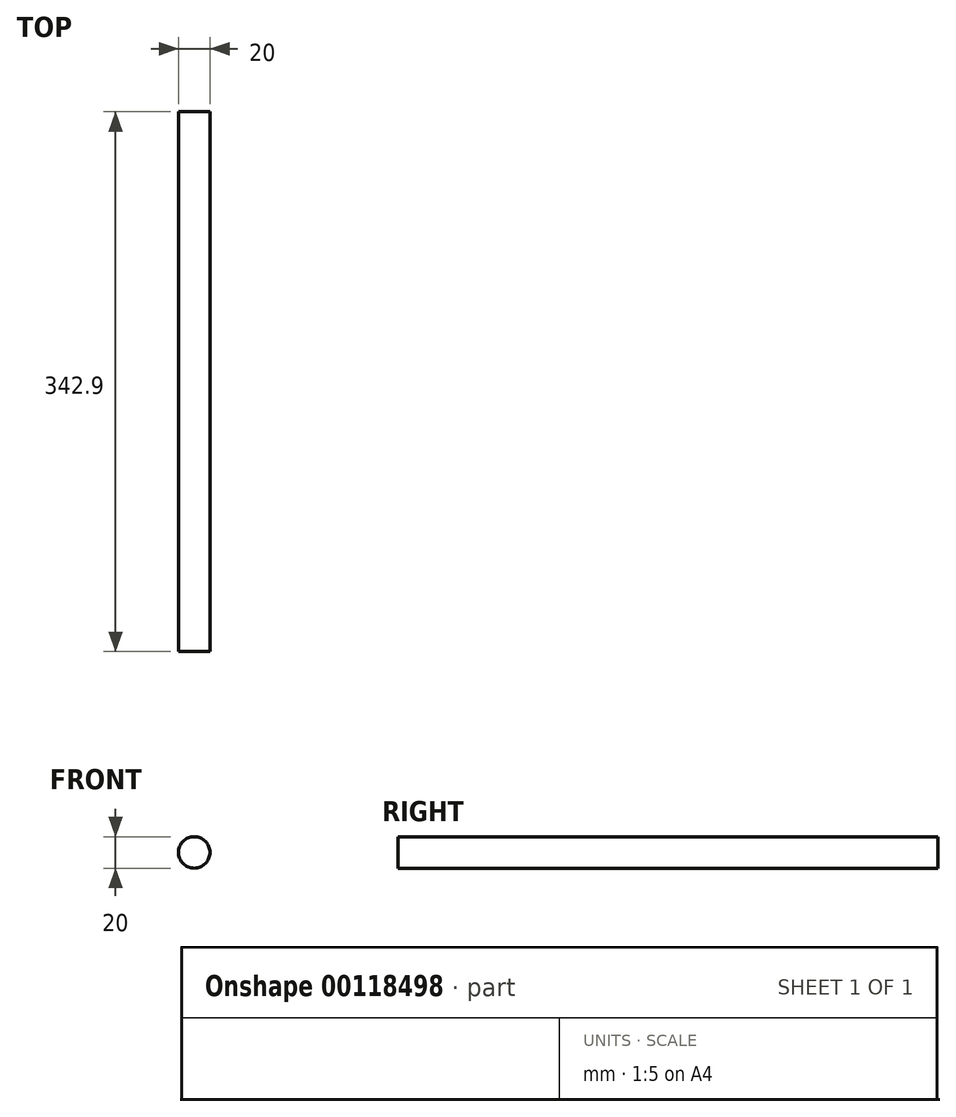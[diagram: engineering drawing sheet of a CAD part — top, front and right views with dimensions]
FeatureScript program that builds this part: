
annotation { "Feature Type Name" : "Feature", "Feature Type Description" : "" }
export const myFeature = defineFeature(function(context is Context, id is Id, definition is map)
    precondition{}
    {
        {
            var Q0;
            Q0=qCreatedBy(makeId("Front.planeOp"),FACE);
            var sketch = newSketch(context, id + "F0", { "sketchPlane" : qUnion([Q0])});
            skCircle(sketch, "E0", {"center": v(0, 0) * mm, "radius": 10 * mm});
            skSolve(sketch);
        }
        {
            var Q0;
            Q0=makeQuery(id+"F0.imprint","IMPRINT",FACE,{"disambiguationData":[TD([[makeQuery(id+"F0.imprint","IMPRINT",EDGE,{"derivedFrom":sQuery(id+"F0.wireOp",EDGE,"E0")}),1.0]])]});
            extrude(context, id + "F1", {"entities" : qUnion([Q0]), "depth" : 342.9 * mm});
        }
    });
